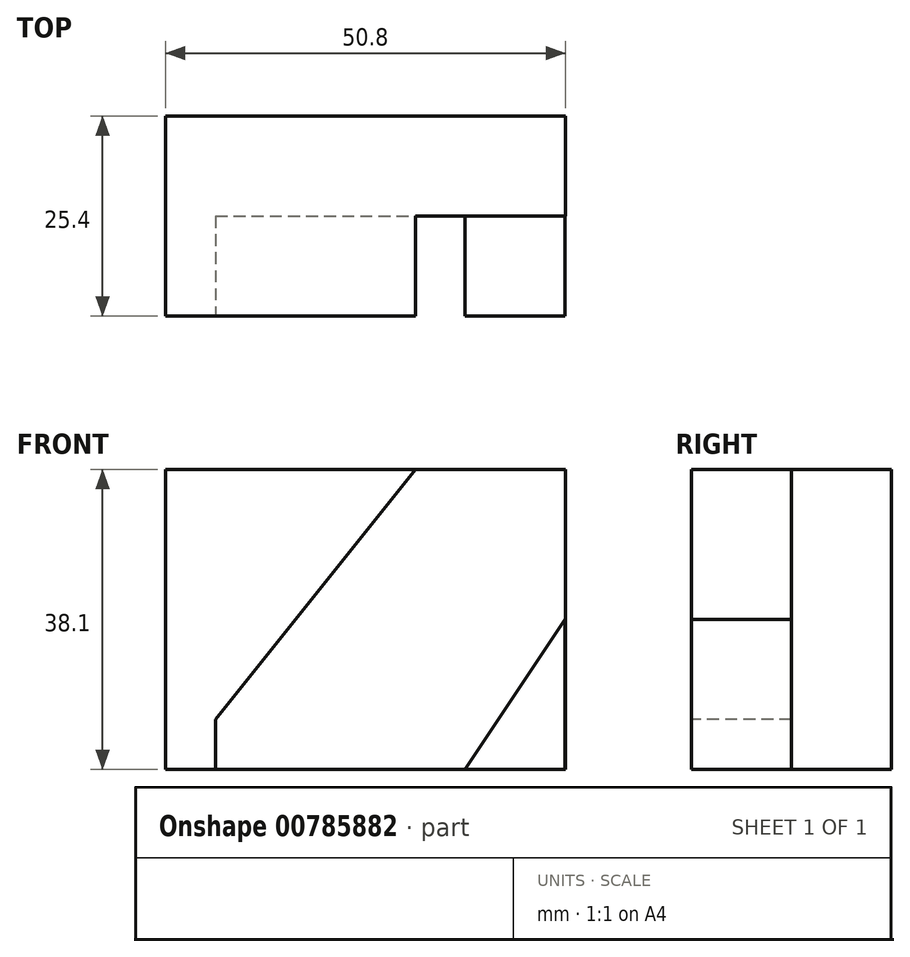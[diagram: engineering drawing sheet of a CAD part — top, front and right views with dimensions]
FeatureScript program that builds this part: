
annotation { "Feature Type Name" : "Feature", "Feature Type Description" : "" }
export const myFeature = defineFeature(function(context is Context, id is Id, definition is map)
    precondition{}
    {
        {
            var Q0;
            Q0=qCreatedBy(makeId("Front.planeOp"),FACE);
            var sketch = newSketch(context, id + "F0", { "sketchPlane" : qUnion([Q0])});
            skLineSegment(sketch, "E0", {"start": v(0, 0) * mm, "end": v(50.8, 0) * mm});
            skLineSegment(sketch, "E1", {"start": v(0, 0) * mm, "end": v(0, 38.1) * mm});
            skLineSegment(sketch, "E2", {"start": v(0, 38.1) * mm, "end": v(50.8, 38.1) * mm});
            skLineSegment(sketch, "E3", {"start": v(50.8, 38.1) * mm, "end": v(50.8, 0) * mm});
            skSolve(sketch);
        }
        {
            var Q0;
            Q0=makeQuery(id+"F0.imprint","IMPRINT",FACE,{"disambiguationData":[TD([[makeQuery(id+"F0.imprint","IMPRINT",EDGE,{"derivedFrom":sQuery(id+"F0.wireOp",EDGE,"E0")}),1.0]])]});
            extrude(context, id + "F1", {"entities" : qUnion([Q0]), "depth" : 25.4 * mm, "offsetDistance" : 25.4 * mm});
        }
        {
            var Q0;
            Q0=makeQuery(id+"F1.opExtrude","CAP_FACE",FACE,{"disambiguationData":[OSD([sQuery(id+"F0.wireOp",EDGE,"E0"),sQuery(id+"F0.wireOp",EDGE,"E1"),sQuery(id+"F0.wireOp",EDGE,"E2"),sQuery(id+"F0.wireOp",EDGE,"E3")])],"isStart":false});
            var sketch = newSketch(context, id + "F2", { "sketchPlane" : qUnion([Q0])});
            skLineSegment(sketch, "E4", {"start": v(0, 0) * mm, "end": v(6.35, 0) * mm});
            skLineSegment(sketch, "E5", {"start": v(50.8, 38.1) * mm, "end": v(31.75, 38.1) * mm});
            skLineSegment(sketch, "E6", {"start": v(6.35, 6.35) * mm, "end": v(31.75, 38.1) * mm});
            skLineSegment(sketch, "E7", {"start": v(6.35, 0) * mm, "end": v(6.35, 6.35) * mm});
            skSolve(sketch);
        }
        {
            var Q0;
            Q0=makeQuery(id+"F2.imprint","IMPRINT",FACE,{"disambiguationData":[TD([[makeQuery(id+"F2.imprint","IMPRINT",EDGE,{"derivedFrom":sQuery(id+"F2.wireOp",EDGE,"E5")}),-1.0]])]});
            var sketch = newSketch(context, id + "F3", { "sketchPlane" : qUnion([Q0])});
            skLineSegment(sketch, "E8", {"start": v(50.71, 0) * mm, "end": v(38.01, 0) * mm});
            skLineSegment(sketch, "E9", {"start": v(50.71, 0) * mm, "end": v(50.71, 19.05) * mm});
            skLineSegment(sketch, "E10", {"start": v(38.01, 0) * mm, "end": v(50.71, 19.05) * mm});
            skSolve(sketch);
        }
        {
            var Q0;
            {var subQ1=sQuery(id+"F3.wireOp",EDGE,"E9");Q0=makeQuery(id+"F3.imprint","IMPRINT",FACE,{"disambiguationData":[TD([[makeQuery(id+"F3.imprint","IMPRINT",EDGE,{"derivedFrom":subQ1}),-1.0]])]});}
            var sketch = newSketch(context, id + "F4", { "sketchPlane" : qUnion([Q0])});
            skLineSegment(sketch, "E11", {"start": v(6.55, 0) * mm, "end": v(38.07, 0) * mm});
            skLineSegment(sketch, "E12", {"start": v(50.86, 18.88) * mm, "end": v(50.86, 37.93) * mm});
            skLineSegment(sketch, "E13", {"start": v(31.65, 37.93) * mm, "end": v(50.86, 37.93) * mm});
            skSolve(sketch);
        }
        {
            var Q0;
            {var subQ2=sQuery(id+"F3.wireOp",EDGE,"E9");Q0=makeQuery(id+"F4.imprint","IMPRINT",FACE,{"disambiguationData":[TD([[makeQuery(id+"F4.imprint","IMPRINT",EDGE,{"derivedFrom":makeQuery(id+"F3.imprint","IMPRINT",EDGE,{"derivedFrom":subQ2})}),-1.0]])]});}
            extrude(context, id + "F5", {"entities" : qUnion([Q0]), "operationType" : NewBodyOperationType.REMOVE, "oppositeDirection" : true, "depth" : 12.7 * mm, "offsetDistance" : 25.4 * mm});
        }
    });
